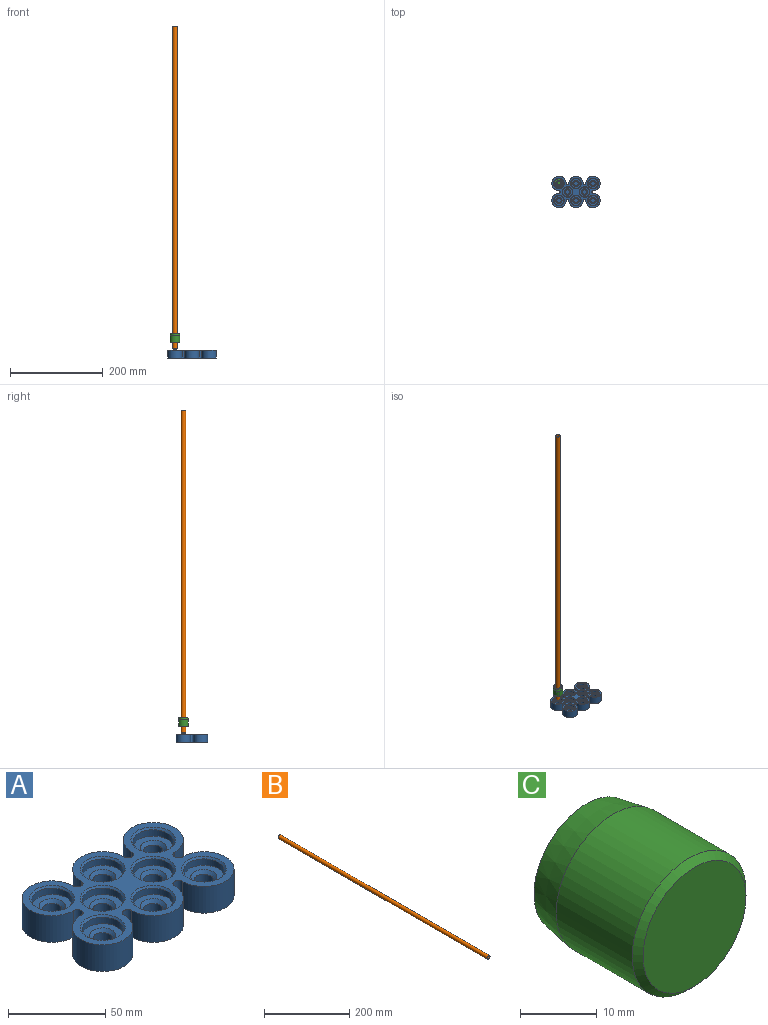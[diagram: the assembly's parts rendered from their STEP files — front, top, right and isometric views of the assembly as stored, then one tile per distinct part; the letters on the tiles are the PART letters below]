
ASSEMBLY  parts=3 mates=2
PART A: 62 faces, bbox 104.5x67.8x16.8 mm
  f0: plane 104.54x67.77mm, normal (0,0,1), area 2320.8mm2, adj f2,f3,f4,f5,f11,f17,f23,f29
  f1: plane 104.54x67.77mm, normal (0,0,-1), area 5644.6mm2, adj f2,f3,f4,f5,f54,f55,f56,f57
  f2: cylinder r=15.5mm len=31mm, axis (0,0,1), area 1223.5mm2, adj f0,f1,f56,f61
  f3: cylinder r=15.5mm len=31mm, axis (0,0,-1), area 1223.5mm2, adj f0,f1,f57,f59
  f4: cylinder r=15.5mm len=31mm, axis (0,0,1), area 1223.5mm2, adj f0,f1,f59,f60
  f5: cylinder r=15.5mm len=31mm, axis (0,0,-1), area 1223.5mm2, adj f0,f1,f54,f56
  f6: cylinder r=10.5mm len=21mm, axis (0,0,1), area 263.9mm2, adj f7,f11
  f7: plane 21x21mm, normal (0,0,1), area 203.2mm2, adj f6,f10
  f8: cylinder r=5mm len=10mm, axis (0,0,1), area 157.1mm2, adj f9,f10
  f9: plane 10x10mm, normal (0,0,1), area 78.5mm2, adj f8
  f10: cone r=5mm half-angle=45deg, axis (0,0,1), area 91.4mm2, adj f7,f8
  f11: cone r=10.5mm half-angle=45deg, axis (0,0,1), area 97.7mm2, adj f0,f6
  f12: cylinder r=10.5mm len=21mm, axis (0,0,1), area 263.9mm2, adj f13,f17
  f13: plane 21x21mm, normal (0,0,1), area 203.2mm2, adj f12,f16
  f14: cylinder r=5mm len=10mm, axis (0,0,1), area 157.1mm2, adj f15,f16
  f15: plane 10x10mm, normal (0,0,1), area 78.5mm2, adj f14
  f16: cone r=5mm half-angle=45deg, axis (0,0,1), area 91.4mm2, adj f13,f14
  f17: cone r=10.5mm half-angle=45deg, axis (0,0,1), area 97.7mm2, adj f0,f12
  f18: cylinder r=10.5mm len=21mm, axis (0,0,1), area 263.9mm2, adj f19,f23
  f19: plane 21x21mm, normal (0,0,1), area 203.2mm2, adj f18,f22
  f20: cylinder r=5mm len=10mm, axis (0,0,1), area 157.1mm2, adj f21,f22
  f21: plane 10x10mm, normal (0,0,1), area 78.5mm2, adj f20
  f22: cone r=5mm half-angle=45deg, axis (0,0,1), area 91.4mm2, adj f19,f20
  f23: cone r=10.5mm half-angle=45deg, axis (0,0,1), area 97.7mm2, adj f0,f18
  f24: cylinder r=10.5mm len=21mm, axis (0,0,1), area 263.9mm2, adj f25,f29
  f25: plane 21x21mm, normal (0,0,1), area 203.2mm2, adj f24,f28
  f26: cylinder r=5mm len=10mm, axis (0,0,1), area 157.1mm2, adj f27,f28
  f27: plane 10x10mm, normal (0,0,1), area 78.5mm2, adj f26
  f28: cone r=5mm half-angle=45deg, axis (0,0,1), area 91.4mm2, adj f25,f26
  f29: cone r=10.5mm half-angle=45deg, axis (0,0,1), area 97.7mm2, adj f0,f24
  f30: cylinder r=10.5mm len=21mm, axis (0,0,1), area 263.9mm2, adj f31,f35
  f31: plane 21x21mm, normal (0,0,1), area 203.2mm2, adj f30,f34
  f32: cylinder r=5mm len=10mm, axis (0,0,1), area 157.1mm2, adj f33,f34
  f33: plane 10x10mm, normal (0,0,1), area 78.5mm2, adj f32
  f34: cone r=5mm half-angle=45deg, axis (0,0,1), area 91.4mm2, adj f31,f32
  f35: cone r=10.5mm half-angle=45deg, axis (0,0,1), area 97.7mm2, adj f0,f30
  f36: cylinder r=10.5mm len=21mm, axis (0,0,1), area 263.9mm2, adj f37,f41
  f37: plane 21x21mm, normal (0,0,1), area 203.2mm2, adj f36,f40
  f38: cylinder r=5mm len=10mm, axis (0,0,1), area 157.1mm2, adj f39,f40
  f39: plane 10x10mm, normal (0,0,1), area 78.5mm2, adj f38
  f40: cone r=5mm half-angle=45deg, axis (0,0,1), area 91.4mm2, adj f37,f38
  f41: cone r=10.5mm half-angle=45deg, axis (0,0,1), area 97.7mm2, adj f0,f36
  f42: cylinder r=10.5mm len=21mm, axis (0,0,1), area 263.9mm2, adj f43,f47
  f43: plane 21x21mm, normal (0,0,1), area 203.2mm2, adj f42,f46
  f44: cylinder r=5mm len=10mm, axis (0,0,1), area 157.1mm2, adj f45,f46
  f45: plane 10x10mm, normal (0,0,1), area 78.5mm2, adj f44
  f46: cone r=5mm half-angle=45deg, axis (0,0,1), area 91.4mm2, adj f43,f44
  f47: cone r=10.5mm half-angle=45deg, axis (0,0,1), area 97.7mm2, adj f0,f42
  f48: cylinder r=10.5mm len=21mm, axis (0,0,1), area 263.9mm2, adj f49,f53
  f49: plane 21x21mm, normal (0,0,1), area 203.2mm2, adj f48,f52
  f50: cylinder r=5mm len=10mm, axis (0,0,1), area 157.1mm2, adj f51,f52
  f51: plane 10x10mm, normal (0,0,1), area 78.5mm2, adj f50
  f52: cone r=5mm half-angle=45deg, axis (0,0,1), area 91.4mm2, adj f49,f50
  f53: cone r=10.5mm half-angle=45deg, axis (0,0,1), area 97.7mm2, adj f0,f48
  f54: cylinder r=2.88mm len=16.75mm, axis (0,0,1), area 151.8mm2, adj f0,f1,f5,f55
  f55: cylinder r=15.5mm len=31mm, axis (0,0,1), area 815.6mm2, adj f0,f1,f54,f60
  f56: cylinder r=2.88mm len=16.75mm, axis (0,0,1), area 151.8mm2, adj f0,f1,f2,f5
  f57: cylinder r=2.88mm len=16.75mm, axis (0,0,1), area 151.8mm2, adj f0,f1,f3,f58
  f58: cylinder r=15.5mm len=31mm, axis (0,0,1), area 815.6mm2, adj f0,f1,f57,f61
  f59: cylinder r=2.88mm len=16.75mm, axis (0,0,1), area 151.8mm2, adj f0,f1,f3,f4
  f60: cylinder r=2.88mm len=16.75mm, axis (0,0,1), area 151.8mm2, adj f0,f1,f4,f55
  f61: cylinder r=2.88mm len=16.75mm, axis (0,0,1), area 151.8mm2, adj f0,f1,f2,f58
PART B: 4 faces, bbox 10x696x10 mm
  f0: cylinder r=4mm len=696mm, axis (0,-1,0), area 17492.4mm2, adj f2,f3
  f1: cylinder r=5mm len=694mm, axis (0,-1,0), area 21802.7mm2, adj f2,f3
  f2: cone r=5mm half-angle=45deg, axis (0,-1,0), area 40mm2, adj f0,f1
  f3: cone r=4mm half-angle=45deg, axis (0,1,0), area 40mm2, adj f0,f1
PART C: 32 faces, bbox 21x20x21 mm
  f0: cylinder r=6.7mm len=13.4mm, axis (0,-1,0), area 105.2mm2, adj f24,f31
  f1: cylinder r=6.7mm len=13.4mm, axis (0,-1,0), area 105.2mm2, adj f29,f30
  f2: cylinder r=10.5mm len=21mm, axis (0,-1,0), area 923.6mm2, adj f5,f6
  f3: plane 19.24x19.24mm, normal (0,1,0), area 136.7mm2, adj f5,f30
  f4: plane 19x19mm, normal (0,-1,0), area 283.5mm2, adj f6
  f5: cone r=10.5mm half-angle=10deg, axis (0,-1,0), area 320.9mm2, adj f2,f3
  f6: cone r=9.5mm half-angle=45deg, axis (0,1,0), area 88.9mm2, adj f2,f4
  f7: plane 16.1x16.1mm, normal (0,1,0), area 58.3mm2, adj f19,f28
  f8: plane 16.1x16.1mm, normal (0,-1,0), area 58.3mm2, adj f18,f29
  f9: cylinder r=8.35mm len=16.7mm, axis (0,1,0), area 115.4mm2, adj f18,f19
  f10: cylinder r=6.7mm len=13.4mm, axis (0,-1,0), area 113.7mm2, adj f27,f28
  f11: plane 16.1x16.1mm, normal (0,1,0), area 58.3mm2, adj f21,f26
  f12: plane 16.1x16.1mm, normal (0,-1,0), area 58.3mm2, adj f20,f27
  f13: cylinder r=8.35mm len=16.7mm, axis (0,1,0), area 115.4mm2, adj f20,f21
  f14: cylinder r=6.7mm len=13.4mm, axis (0,-1,0), area 113.7mm2, adj f25,f26
  f15: plane 16.1x16.1mm, normal (0,1,0), area 58.3mm2, adj f23,f24
  f16: plane 16.1x16.1mm, normal (0,-1,0), area 58.3mm2, adj f22,f25
  f17: cylinder r=8.35mm len=16.7mm, axis (0,1,0), area 115.4mm2, adj f22,f23
  f18: torus R=8.05mm, axis (0,1,0), area 24.4mm2, adj f8,f9
  f19: torus R=8.05mm, axis (0,1,0), area 24.4mm2, adj f7,f9
  f20: torus R=8.05mm, axis (0,1,0), area 24.4mm2, adj f12,f13
  f21: torus R=8.05mm, axis (0,1,0), area 24.4mm2, adj f11,f13
  f22: torus R=8.05mm, axis (0,1,0), area 24.4mm2, adj f16,f17
  f23: torus R=8.05mm, axis (0,1,0), area 24.4mm2, adj f15,f17
  f24: torus R=6.8mm, axis (0,1,0), area 6.6mm2, adj f0,f15
  f25: torus R=6.8mm, axis (0,1,0), area 6.6mm2, adj f14,f16
  f26: torus R=6.8mm, axis (0,1,0), area 6.6mm2, adj f11,f14
  f27: torus R=6.8mm, axis (0,1,0), area 6.6mm2, adj f10,f12
  f28: torus R=6.8mm, axis (0,1,0), area 6.6mm2, adj f7,f10
  f29: torus R=6.8mm, axis (0,1,0), area 6.6mm2, adj f1,f8
  f30: cone r=7mm half-angle=45deg, axis (0,1,0), area 18.3mm2, adj f1,f3
  f31: plane 13.4x13.4mm, normal (0,1,0), area 141mm2, adj f0
PLACE A rot(axis=(0,0,1),0deg) t=(-21.38,-8.28,-0.37)mm
PLACE B rot(axis=(1,0,0),90deg) t=(-5.88,43.99,18.65)mm
PLACE C rot(axis=(1,0,0),90deg) t=(-5.88,43.99,32.38)mm
MATE slider C.f2 <-> A.f5  axis (0,0,-1) through (-5.88,43.99,33.38)mm
MATE slider B.f0 <-> C.f0  axis (0,0,-1) through (-5.88,43.99,18.65)mm
